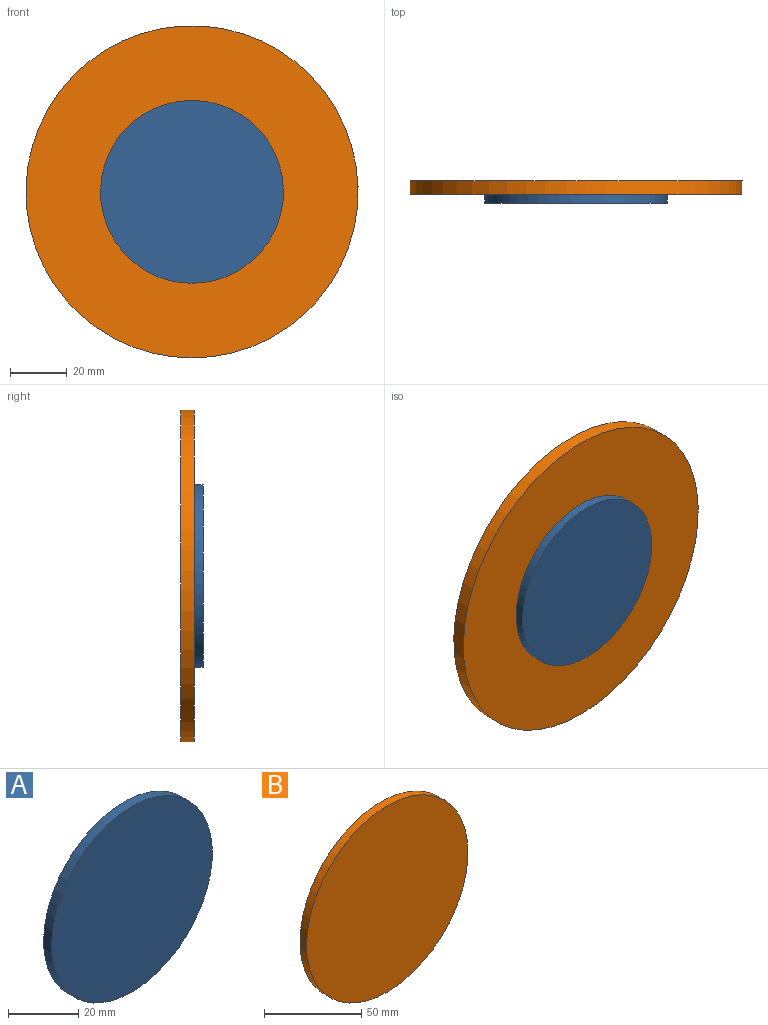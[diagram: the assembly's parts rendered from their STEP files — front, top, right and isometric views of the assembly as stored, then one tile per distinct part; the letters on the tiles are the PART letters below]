
ASSEMBLY  parts=2 mates=1
PART A: 3 faces, bbox 64.6x3.2x64.6 mm
  f0: cylinder r=32.3mm len=64.61mm, axis (0,1,0), area 644.4mm2, adj f1,f2
  f1: plane 64.61x64.61mm, normal (0,-1,0), area 3278.4mm2, adj f0
  f2: plane 64.61x64.61mm, normal (0,1,0), area 3278.4mm2, adj f0
PART B: 3 faces, bbox 117.4x4.8x117.4 mm
  f0: cylinder r=58.7mm len=117.41mm, axis (0,1,0), area 1756.6mm2, adj f1,f2
  f1: plane 117.41x117.41mm, normal (0,-1,0), area 10826.4mm2, adj f0
  f2: plane 117.41x117.41mm, normal (0,1,0), area 10826.4mm2, adj f0
PLACE A rot(axis=(0.58,-0.37,-0.72),0deg) t=(-9.09,-4.67,-10.44)mm
PLACE B rot(axis=(0.55,-0.49,-0.68),0deg) t=(-9.09,0.09,-10.44)mm
MATE revolute A.f0 <-> B.f0  axis (0,1,0) through (-9.09,-4.67,-10.44)mm
